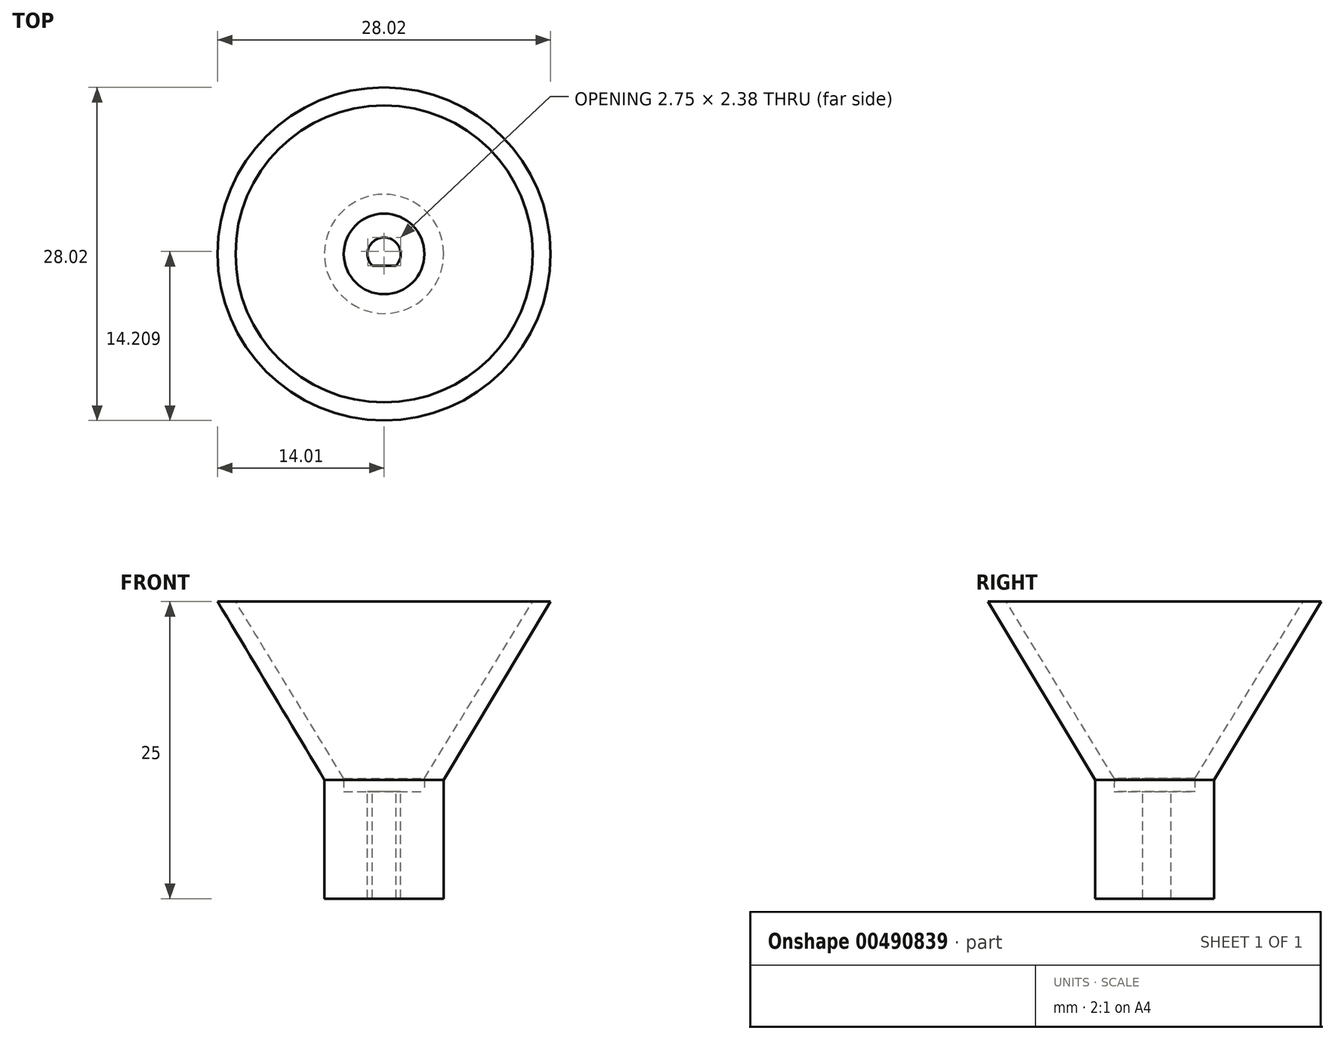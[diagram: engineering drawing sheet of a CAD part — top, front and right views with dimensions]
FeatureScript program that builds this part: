
annotation { "Feature Type Name" : "Feature", "Feature Type Description" : "" }
export const myFeature = defineFeature(function(context is Context, id is Id, definition is map)
    precondition{}
    {
        {
            var Q0;
            Q0=qCreatedBy(makeId("Top.planeOp"),FACE);
            var sketch = newSketch(context, id + "F0", { "sketchPlane" : qUnion([Q0])});
            skLineSegment(sketch, "E0.top", {"start": v(1, -0.99) * mm, "end": v(-1, -0.99) * mm});
            skPoint(sketch, "E0.middle", {"position": v(0, 0) * mm});
            skArc(sketch, "E1", {"start": v(1, -0.99) * mm, "mid": v(1.21, -0.71) * mm, "end": v(1.35, -0.4) * mm});
            skPoint(sketch, "E1.first.point", {"position": v(-1.38, 0.2) * mm});
            skPoint(sketch, "E1.second.point", {"position": v(1.38, 0.2) * mm});
            skPoint(sketch, "E1.third.point", {"position": v(0.1, 1.38) * mm});
            skArc(sketch, "E2.trimOffspring", {"start": v(-0.13, 1.38) * mm, "mid": v(-1.31, 0.47) * mm, "end": v(-1, -0.99) * mm});
            skArc(sketch, "E3.trimOffspring", {"start": v(1.38, 0.2) * mm, "mid": v(0.95, 1.01) * mm, "end": v(0.1, 1.38) * mm});
            skArc(sketch, "E4", {"start": v(-0.13, 1.38) * mm, "mid": v(0, 1.39) * mm, "end": v(0.1, 1.38) * mm});
            skArc(sketch, "E5", {"start": v(1.38, 0.2) * mm, "mid": v(1.4, -0.1) * mm, "end": v(1.35, -0.4) * mm});
            skCircle(sketch, "E6", {"center": v(0, 0) * mm, "radius": 5.01 * mm});
            skSolve(sketch);
        }
        {
            var Q0;
            Q0=qCreatedBy(makeId("Right.planeOp"),FACE);
            var sketch = newSketch(context, id + "F1", { "sketchPlane" : qUnion([Q0])});
            skLineSegment(sketch, "E7", {"start": v(5.01, 1) * mm, "end": v(14, 16) * mm});
            skLineSegment(sketch, "E8", {"start": v(14, 16) * mm, "end": v(12.5, 16) * mm});
            skLineSegment(sketch, "E9", {"start": v(12.5, 16) * mm, "end": v(3.32, 1) * mm});
            skLineSegment(sketch, "E10", {"start": v(5.01, 1) * mm, "end": v(5.01, 0) * mm});
            skLineSegment(sketch, "E11", {"start": v(5.01, 0) * mm, "end": v(3.4, 0) * mm});
            skLineSegment(sketch, "E12", {"start": v(3.4, 0) * mm, "end": v(3.4, 1.11) * mm});
            skSolve(sketch);
        }
        {
            var Q0;
            Q0=makeQuery(id+"F0.imprint","IMPRINT",FACE,{"disambiguationData":[TD([[makeQuery(id+"F0.imprint","IMPRINT",EDGE,{"derivedFrom":sQuery(id+"F0.wireOp",EDGE,"E0.top")}),1.0]])]});
            extrude(context, id + "F2", {"entities" : qUnion([Q0]), "oppositeDirection" : true, "depth" : 9 * mm});
        }
        {
            var Q0;
            Q0=makeQuery(id+"F1.imprint","IMPRINT",FACE,{"disambiguationData":[TD([[makeQuery(id+"F1.imprint","IMPRINT",EDGE,{"derivedFrom":sQuery(id+"F1.wireOp",EDGE,"E7")}),1.0]])]});
            var Q1;
            Q1=makeQuery(id+"F2.opExtrude","CAP_EDGE",EDGE,{"disambiguationData":[OSD([sQuery(id+"F0.wireOp",EDGE,"E6")])],"isStart":true});
            revolve(context, id + "F3", {"operationType" : NewBodyOperationType.ADD, "entities" : qUnion([Q0]), "axis" : qUnion([Q1]), "revolveType" : RevolveType.FULL});
        }
    });
